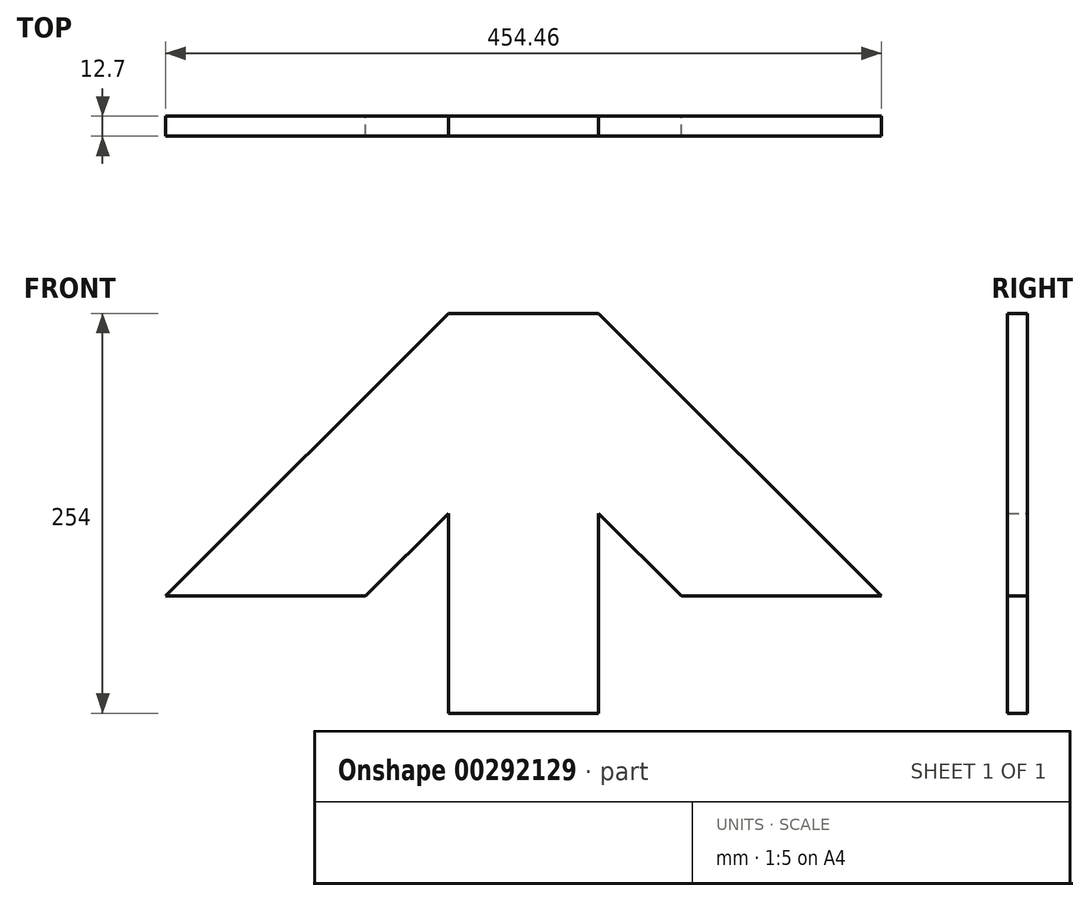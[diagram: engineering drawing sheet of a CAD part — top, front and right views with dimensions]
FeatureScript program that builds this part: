
annotation { "Feature Type Name" : "Feature", "Feature Type Description" : "" }
export const myFeature = defineFeature(function(context is Context, id is Id, definition is map)
    precondition{}
    {
        {
            var Q0;
            Q0=qCreatedBy(makeId("Front.planeOp"),FACE);
            var sketch = newSketch(context, id + "F0", { "sketchPlane" : qUnion([Q0])});
            skLineSegment(sketch, "E0", {"start": v(-47.63, 127) * mm, "end": v(47.62, 127) * mm});
            skLineSegment(sketch, "E1", {"start": v(47.62, 127) * mm, "end": v(227.23, -52.6) * mm});
            skLineSegment(sketch, "E2", {"start": v(227.23, -52.6) * mm, "end": v(100.23, -52.6) * mm});
            skLineSegment(sketch, "E3", {"start": v(100.23, -52.6) * mm, "end": v(47.62, 0) * mm});
            skLineSegment(sketch, "E4", {"start": v(47.62, 0) * mm, "end": v(47.62, -127) * mm});
            skLineSegment(sketch, "E5", {"start": v(47.62, -127) * mm, "end": v(-47.62, -127) * mm});
            skLineSegment(sketch, "E6", {"start": v(-47.63, -127) * mm, "end": v(-47.63, 0) * mm});
            skLineSegment(sketch, "E7", {"start": v(-47.62, 0) * mm, "end": v(-100.23, -52.6) * mm});
            skLineSegment(sketch, "E8", {"start": v(-100.23, -52.6) * mm, "end": v(-227.23, -52.6) * mm});
            skLineSegment(sketch, "E9", {"start": v(-227.23, -52.6) * mm, "end": v(-47.62, 127) * mm});
            skSolve(sketch);
        }
        {
            var Q0;
            Q0=makeQuery(id+"F0.imprint","IMPRINT",FACE,{"disambiguationData":[TD([[makeQuery(id+"F0.imprint","IMPRINT",EDGE,{"derivedFrom":sQuery(id+"F0.wireOp",EDGE,"E0")}),-1.0]])]});
            extrude(context, id + "F1", {"entities" : qUnion([Q0]), "depth" : 12.7 * mm});
        }
    });
